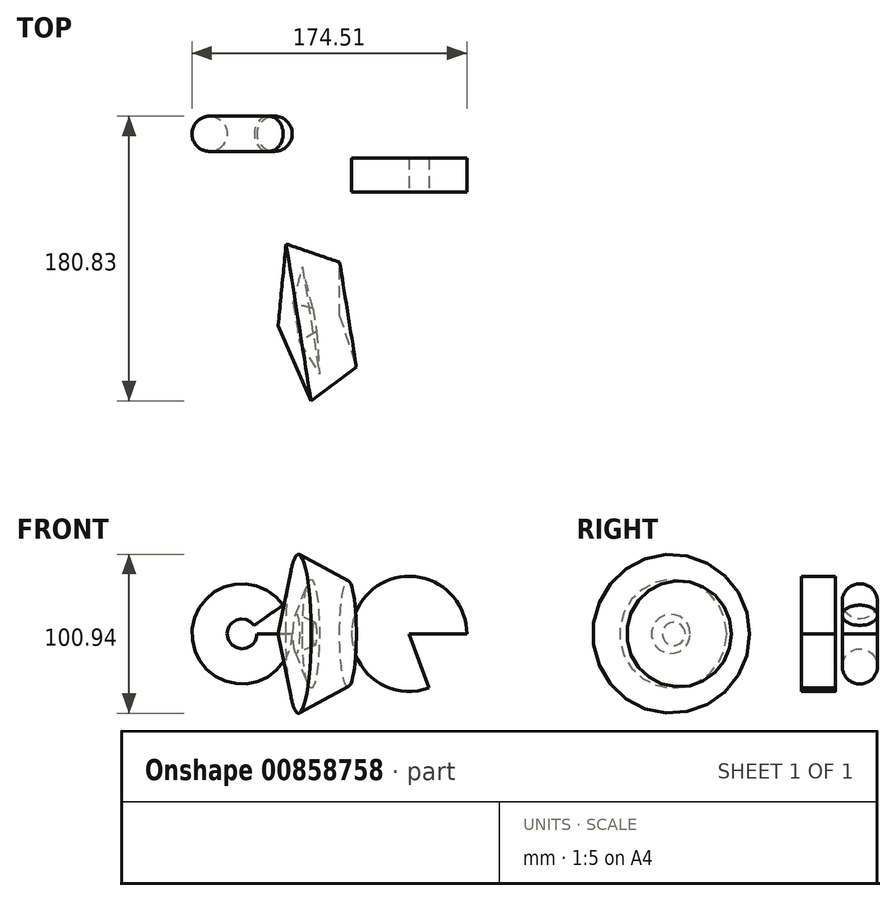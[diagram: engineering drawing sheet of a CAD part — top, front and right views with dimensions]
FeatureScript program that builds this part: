
annotation { "Feature Type Name" : "Feature", "Feature Type Description" : "" }
export const myFeature = defineFeature(function(context is Context, id is Id, definition is map)
    precondition{}
    {
        {
            var Q0;
            Q0=qCreatedBy(makeId("Top.planeOp"),FACE);
            var sketch = newSketch(context, id + "F0", { "sketchPlane" : qUnion([Q0])});
            skCircle(sketch, "E0", {"center": v(-62.28, 52.52) * mm, "radius": 11.18 * mm});
            skLineSegment(sketch, "E1.bottom", {"start": v(23.25, 37.16) * mm, "end": v(59.79, 37.16) * mm});
            skLineSegment(sketch, "E1.top", {"start": v(23.25, 15.57) * mm, "end": v(59.79, 15.57) * mm});
            skLineSegment(sketch, "E1.left", {"start": v(23.25, 37.16) * mm, "end": v(23.25, 15.57) * mm});
            skLineSegment(sketch, "E1.right", {"start": v(59.79, 37.16) * mm, "end": v(59.79, 15.57) * mm});
            skLineSegment(sketch, "E2", {"start": v(-55, -17.45) * mm, "end": v(-20.95, -29.08) * mm});
            skLineSegment(sketch, "E3", {"start": v(-20.95, -29.08) * mm, "end": v(-20.95, -63.13) * mm});
            skLineSegment(sketch, "E4", {"start": v(-20.95, -63.13) * mm, "end": v(-59.98, -69.35) * mm});
            skLineSegment(sketch, "E5", {"start": v(-59.98, -69.35) * mm, "end": v(-55, -17.45) * mm});
            skLineSegment(sketch, "E6", {"start": v(-44.62, -31.99) * mm, "end": v(-50.43, -55.24) * mm});
            skLineSegment(sketch, "E7", {"start": v(-50.43, -55.24) * mm, "end": v(-37.93, -58.36) * mm});
            skLineSegment(sketch, "E8", {"start": v(-37.93, -58.36) * mm, "end": v(-44.62, -31.99) * mm});
            skLineSegment(sketch, "E9", {"start": v(-82.91, 71.7) * mm, "end": v(-82.91, 30.26) * mm, "construction": true});
            skSolve(sketch);
        }
        {
            var Q0;
            Q0=makeQuery(id+"F0.imprint","IMPRINT",FACE,{"disambiguationData":[TD([[makeQuery(id+"F0.imprint","IMPRINT",EDGE,{"derivedFrom":sQuery(id+"F0.wireOp",EDGE,"E0")}),1.0]])]});
            var Q1;
            Q1=sQuery(id+"F0.wireOp",EDGE,"E9");
            revolve(context, id + "F1", {"surfaceOperationType" : NewSurfaceOperationType.NEW, "entities" : qUnion([Q0]), "axis" : qUnion([Q1]), "revolveType" : RevolveType.ONE_DIRECTION, "oppositeDirection" : true, "angle" : 325 * degree});
        }
        {
            var Q0;
            Q0=makeQuery(id+"F0.imprint","IMPRINT",FACE,{"disambiguationData":[TD([[makeQuery(id+"F0.imprint","IMPRINT",EDGE,{"derivedFrom":sQuery(id+"F0.wireOp",EDGE,"E1.bottom")}),-1.0]])]});
            var Q1;
            Q1=sQuery(id+"F0.wireOp",EDGE,"E1.left");
            revolve(context, id + "F2", {"surfaceOperationType" : NewSurfaceOperationType.NEW, "entities" : qUnion([Q0]), "axis" : qUnion([Q1]), "revolveType" : RevolveType.ONE_DIRECTION, "angle" : 290 * degree});
        }
        {
            var Q0;
            Q0=makeQuery(id+"F0.imprint","IMPRINT",FACE,{"disambiguationData":[TD([[makeQuery(id+"F0.imprint","IMPRINT",EDGE,{"derivedFrom":sQuery(id+"F0.wireOp",EDGE,"E2")}),-1.0]])]});
            var Q1;
            Q1=sQuery(id+"F0.wireOp",EDGE,"E4");
            revolve(context, id + "F3", {"surfaceOperationType" : NewSurfaceOperationType.NEW, "entities" : qUnion([Q0]), "axis" : qUnion([Q1]), "revolveType" : RevolveType.FULL});
        }
    });
